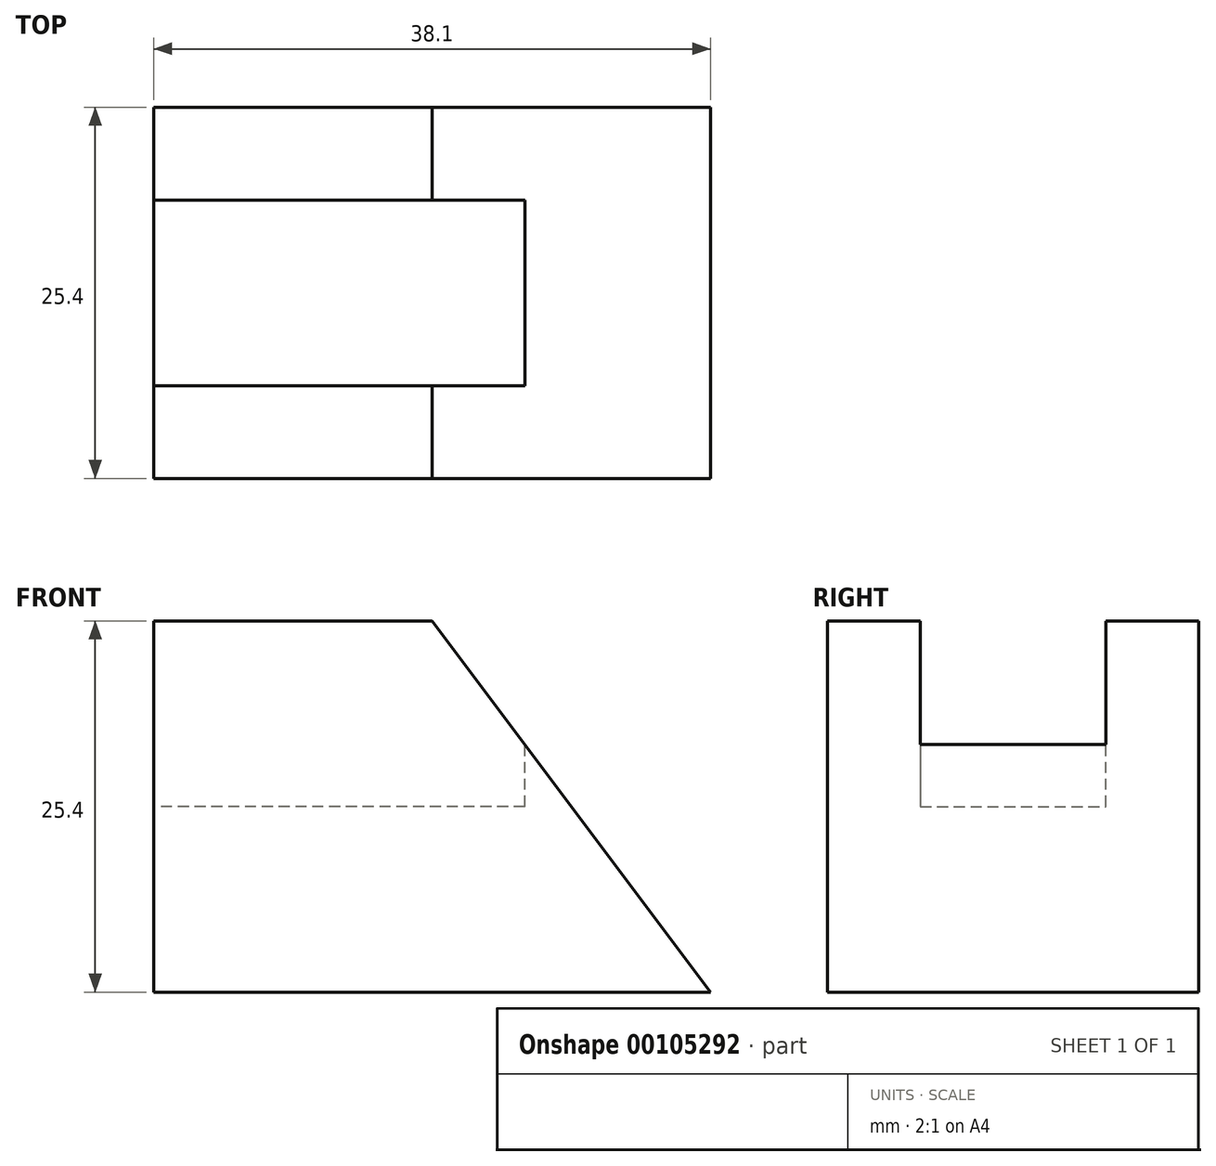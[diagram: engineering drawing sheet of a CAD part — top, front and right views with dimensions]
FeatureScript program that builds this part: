
annotation { "Feature Type Name" : "Feature", "Feature Type Description" : "" }
export const myFeature = defineFeature(function(context is Context, id is Id, definition is map)
    precondition{}
    {
        {
            var Q0;
            Q0=qCreatedBy(makeId("Right.planeOp"),FACE);
            var sketch = newSketch(context, id + "F0", { "sketchPlane" : qUnion([Q0])});
            skLineSegment(sketch, "E0", {"start": v(0, 0) * mm, "end": v(0, 25.4) * mm});
            skLineSegment(sketch, "E1", {"start": v(0, 25.4) * mm, "end": v(6.35, 25.4) * mm});
            skLineSegment(sketch, "E2", {"start": v(6.35, 25.4) * mm, "end": v(6.35, 12.7) * mm});
            skLineSegment(sketch, "E3", {"start": v(6.35, 12.7) * mm, "end": v(19.05, 12.7) * mm});
            skLineSegment(sketch, "E4", {"start": v(19.05, 12.7) * mm, "end": v(19.05, 25.4) * mm});
            skLineSegment(sketch, "E5", {"start": v(19.05, 25.4) * mm, "end": v(25.4, 25.4) * mm});
            skLineSegment(sketch, "E6", {"start": v(25.4, 25.4) * mm, "end": v(25.4, 0) * mm});
            skLineSegment(sketch, "E7", {"start": v(25.4, 0) * mm, "end": v(0, 0) * mm});
            skLineSegment(sketch, "E8", {"start": v(6.35, 25.4) * mm, "end": v(19.05, 25.4) * mm});
            skSolve(sketch);
        }
        {
            var Q0;
            Q0=qCreatedBy(makeId("Front.planeOp"),FACE);
            var sketch = newSketch(context, id + "F1", { "sketchPlane" : qUnion([Q0])});
            skLineSegment(sketch, "E9", {"start": v(0, 25.4) * mm, "end": v(19.05, 25.4) * mm});
            skLineSegment(sketch, "E10", {"start": v(0, 0) * mm, "end": v(38.1, 0) * mm});
            skLineSegment(sketch, "E11", {"start": v(19.05, 25.4) * mm, "end": v(38.1, 0) * mm});
            skLineSegment(sketch, "E12", {"start": v(0, 25.4) * mm, "end": v(0, 0) * mm});
            skSolve(sketch);
        }
        {
            var Q0;
            Q0=makeQuery(id+"F1.imprint","IMPRINT",FACE,{"disambiguationData":[TD([[makeQuery(id+"F1.imprint","IMPRINT",EDGE,{"derivedFrom":sQuery(id+"F1.wireOp",EDGE,"E9")}),-1.0]])]});
            extrude(context, id + "F2", {"entities" : qUnion([Q0]), "oppositeDirection" : true, "depth" : 25.4 * mm});
        }
        {
            var Q0;
            Q0=makeQuery(id+"F0.imprint","IMPRINT",FACE,{"disambiguationData":[TD([[makeQuery(id+"F0.imprint","IMPRINT",EDGE,{"derivedFrom":sQuery(id+"F0.wireOp",EDGE,"E2")}),1.0]])]});
            extrude(context, id + "F3", {"entities" : qUnion([Q0]), "operationType" : NewBodyOperationType.REMOVE, "depth" : 25.4 * mm});
        }
    });
